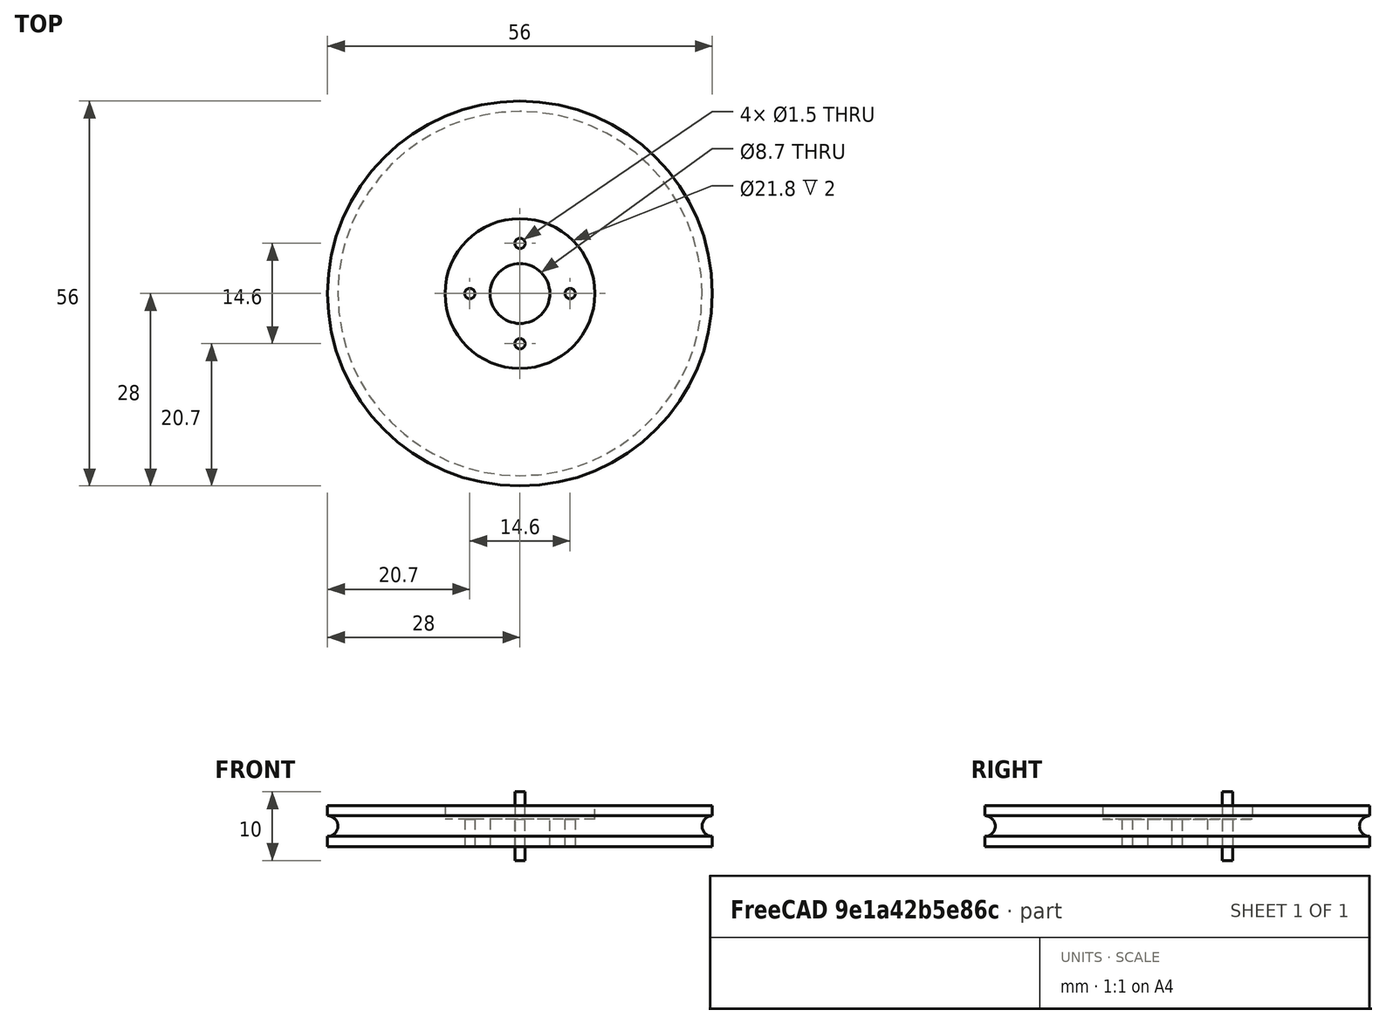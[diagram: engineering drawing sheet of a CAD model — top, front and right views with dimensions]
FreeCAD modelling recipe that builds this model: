
FCSTD DOCUMENT  (FreeCAD 1.0R39319 (Git))
Label: ojt1_t15p01_mini_skybot
License: All rights reserved
LicenseURL: https://en.wikipedia.org/wiki/All_rights_reserved
objects: Part::Cylinder×4, Part::Cut×4, Part::Torus×1, Part::FeaturePython×1
note: 9 computed .brp shape members not serialized (recipe doc carries the construction recipe); baked Part::Feature solids carry a one-line shape summary decoded from their .brp

FEATURE [Part::Cylinder] Cylinder  label="Cilindre"
  Angle = 360
  AttacherType = Attacher::AttachEngine3D
  FirstAngle = 0
  Height = 6
  Placement = pos=(0,0,-3) rot=(0,0,1;0rad)
  Radius = 28
  SecondAngle = 0
FEATURE [Part::Torus] Torus
  Angle1 = -180
  Angle2 = 180
  Angle3 = 360
  AttacherType = Attacher::AttachEngine3D
  Radius1 = 28
  Radius2 = 1.5
FEATURE [Part::Cut] Cut  label="roda_bàsica"
  Base = -> Cylinder
  Tool = -> Torus
FEATURE [Part::Cylinder] Cylinder001  label="Cilindre001"
  Angle = 360
  AttacherType = Attacher::AttachEngine3D
  FirstAngle = 0
  Height = 10
  Placement = pos=(0,0,1) rot=(0,0,1;0rad)
  Radius = 10.9
  SecondAngle = 0
FEATURE [Part::Cut] Cut001  label="roda-amb-forat-rodona"
  Base = -> Cut
  Tool = -> Cylinder001
FEATURE [Part::Cylinder] Cylinder002  label="Cilindre002"
  Angle = 360
  AttacherType = Attacher::AttachEngine3D
  FirstAngle = 0
  Height = 10
  Placement = pos=(0,0,-5) rot=(0,0,1;0rad)
  Radius = 4.35
  SecondAngle = 0
FEATURE [Part::Cut] Cut002  label="roda-corona-eix"
  Base = -> Cut001
  Tool = -> Cylinder002
FEATURE [Part::Cylinder] Cylinder003  label="Cilindre003"
  Angle = 360
  AttacherType = Attacher::AttachEngine3D
  FirstAngle = 0
  Height = 10
  Placement = pos=(0,7.3,-5) rot=(0,0,1;0rad)
  Radius = 0.75
  SecondAngle = 0
FEATURE [Part::FeaturePython] Array  # Draft array (typed FeaturePython)
  AlwaysSyncPlacement = false
  Angle = 360
  ArrayType = 1
  Axis = (0,0,1)
  Base = -> Cylinder003
  Center = (0,0,0)
  Count = 4
  ExpandArray = false
  Fuse = false
  IntervalAxis = (0,0,0)
  IntervalX = (50,0,0)
  IntervalY = (0,50,0)
  IntervalZ = (0,0,50)
  NumberCircles = 3
  NumberPolar = 4
  NumberX = 2
  NumberY = 2
  NumberZ = 1
  PlacementList = 4 placements: [(0,7.3,-5),(-7.3,0,-5),(-8.93992e-16,-7.3,-5),(7.3,-1.62093e-15,-5)]
  RadialDistance = 100
  ScaleList = (4) [(1,1,1),(1,1,1),(1,1,1),(1,1,1)]
  Symmetry = 1
  TangentialDistance = 50
FEATURE [Part::Cut] Cut003  label="roda-finaltizada"
  Base = -> Cut002
  Tool = -> Array
